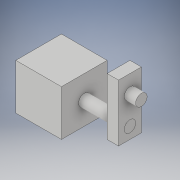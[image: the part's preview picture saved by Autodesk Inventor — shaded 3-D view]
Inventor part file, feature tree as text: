
AUTODESK INVENTOR PART (.ipt)
format: ipt  version: 2019 (Build 230136000, 136)  size: 138,240 bytes
history: native  units: in
note: dims shown in document units (in); Inventor stores cm internally (conversion verified against a paired STEP export)
features: extrude x4, sketch x4
ambient origin geometry x8: Origin, YZ Plane, XZ Plane, XY Plane, X Axis, Y Axis, Z Axis, Center Point
bodies: Solid1 (feature_tree), Solid2 (feature_tree), Solid3 (feature_tree), Solid5 (feature_tree)
feature tree (8):
  extrude  "Extrusion1"  Depth=2.0in
  extrude  "Extrusion2"  Depth=0.5in
  extrude  "Extrusion3"  Depth=1.0in
  extrude  "Extrusion5"  Depth=1.0in
  sketch  "Sketch1"  dims[d0=2.0in d1=2.0in]
  sketch  "Sketch2"  dims[d2=2.0in d3=0.0in d4=0.5in]
  sketch  "Sketch3"  dims[d5=1.0in d6=1.0in]
  sketch  "Sketch5"  dims[d7=2.0in d8=0.0in d9=1.0in d10=2.5in d11=0.5in d12=0.5in d14=0.5in d15=0.0in d16=0.5in d20=0.5in d21=1.0in d22=0.5in d23=0.75in d24=0.5in d25=0.0in]
